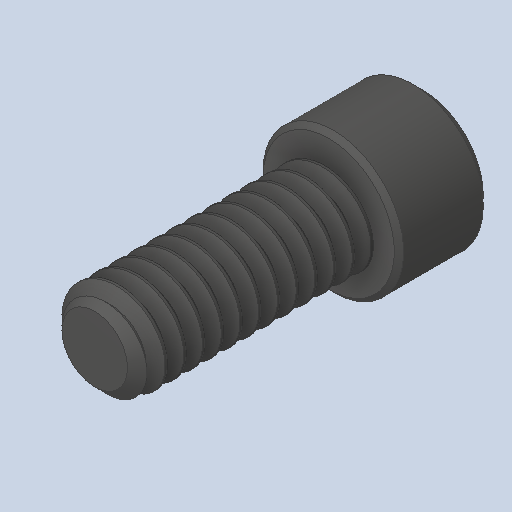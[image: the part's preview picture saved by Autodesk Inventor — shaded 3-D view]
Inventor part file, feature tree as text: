
AUTODESK INVENTOR PART (.ipt)
format: ipt  version: 2023.4 (Build 274418000, 418)  size: 534,528 bytes
history: native  units: in
note: dims shown in document units (in); Inventor stores cm internally (conversion verified against a paired STEP export)
features: chamfer x1
ambient origin geometry x8: Origin, YZ Plane, XZ Plane, XY Plane, X Axis, Y Axis, Z Axis, Center Point
bodies: Solid1 (feature_tree)
feature tree (1):
  chamfer  "Chamfer2"  [1 undecoded]
note: 1 required parameter value undecoded (feature->parameter linkage not recoverable at this tier; creation-order binding heuristic only, values carry confidence <= 0.55)
